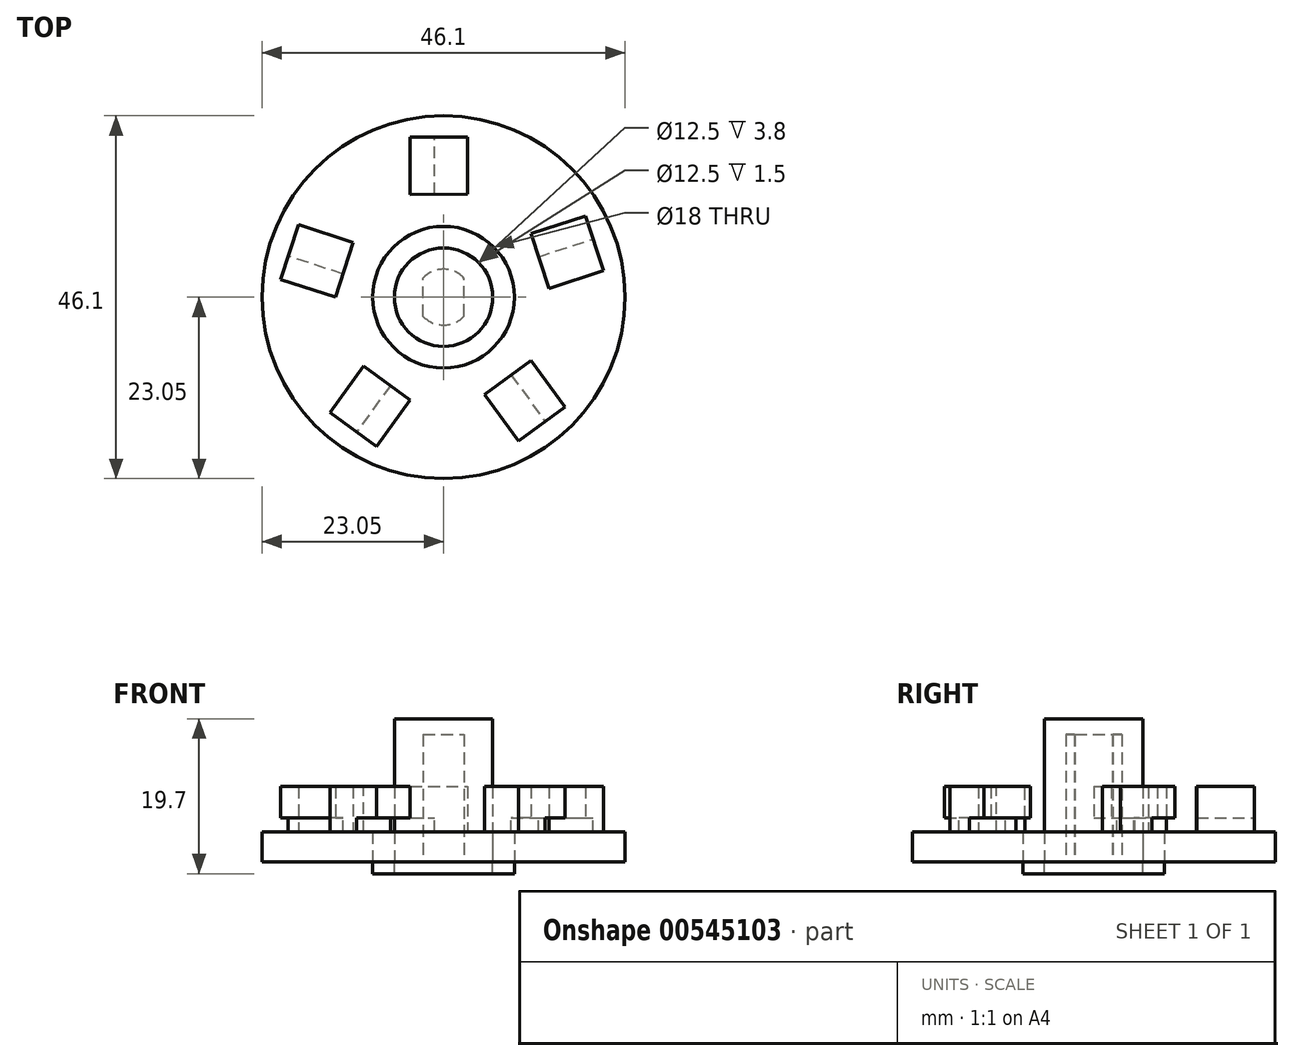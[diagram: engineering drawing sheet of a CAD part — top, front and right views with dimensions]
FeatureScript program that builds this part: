
annotation { "Feature Type Name" : "Feature", "Feature Type Description" : "" }
export const myFeature = defineFeature(function(context is Context, id is Id, definition is map)
    precondition{}
    {
        {
            var Q0;
            Q0=qCreatedBy(makeId("Top.planeOp"),FACE);
            var sketch = newSketch(context, id + "F0", { "sketchPlane" : qUnion([Q0])});
            skCircle(sketch, "E0", {"center": v(0, 0) * mm, "radius": 23.05 * mm});
            skCircle(sketch, "E1", {"center": v(0, 0) * mm, "radius": 6.25 * mm});
            skCircle(sketch, "E2", {"center": v(0, 0) * mm, "radius": 9 * mm});
            skLineSegment(sketch, "E3.left", {"start": v(-2.59, -2.43) * mm, "end": v(-2.59, 2.43) * mm});
            skLineSegment(sketch, "E3.right", {"start": v(2.62, -2.4) * mm, "end": v(2.62, 2.4) * mm});
            skArc(sketch, "E4", {"start": v(2.62, 2.4) * mm, "mid": v(0.03, 3.55) * mm, "end": v(-2.59, 2.43) * mm});
            skArc(sketch, "E5.trimOffspring", {"start": v(-2.59, -2.43) * mm, "mid": v(0.03, -3.55) * mm, "end": v(2.62, -2.4) * mm});
            skLineSegment(sketch, "E6", {"start": v(-1.36, -13.16) * mm, "end": v(-6.58, -20.37) * mm});
            skLineSegment(sketch, "E7", {"start": v(-6.58, -20.37) * mm, "end": v(-10.96, -17.2) * mm});
            skLineSegment(sketch, "E8", {"start": v(-10.96, -17.2) * mm, "end": v(-5.74, -10) * mm});
            skLineSegment(sketch, "E9", {"start": v(-5.74, -10) * mm, "end": v(-1.36, -13.16) * mm});
            skLineSegment(sketch, "E10", {"start": v(-12.94, -2.77) * mm, "end": v(-21.4, -0.04) * mm});
            skLineSegment(sketch, "E11", {"start": v(-21.4, -0.04) * mm, "end": v(-19.75, 5.1) * mm});
            skLineSegment(sketch, "E12", {"start": v(-19.75, 5.1) * mm, "end": v(-11.28, 2.37) * mm});
            skLineSegment(sketch, "E13", {"start": v(-11.28, 2.37) * mm, "end": v(-12.94, -2.77) * mm});
            skLineSegment(sketch, "E14", {"start": v(-6.63, 11.45) * mm, "end": v(-6.65, 20.35) * mm});
            skLineSegment(sketch, "E15", {"start": v(-6.65, 20.35) * mm, "end": v(-1.25, 20.36) * mm});
            skLineSegment(sketch, "E16", {"start": v(-1.25, 20.36) * mm, "end": v(-1.23, 11.46) * mm});
            skLineSegment(sketch, "E17", {"start": v(-1.23, 11.46) * mm, "end": v(-6.63, 11.45) * mm});
            skLineSegment(sketch, "E18", {"start": v(8.84, 9.85) * mm, "end": v(17.3, 12.61) * mm});
            skLineSegment(sketch, "E19", {"start": v(17.3, 12.61) * mm, "end": v(18.98, 7.48) * mm});
            skLineSegment(sketch, "E20", {"start": v(18.98, 7.48) * mm, "end": v(10.52, 4.71) * mm});
            skLineSegment(sketch, "E21", {"start": v(10.52, 4.71) * mm, "end": v(8.84, 9.85) * mm});
            skLineSegment(sketch, "E22", {"start": v(7.73, -8.55) * mm, "end": v(12.98, -15.74) * mm});
            skLineSegment(sketch, "E23", {"start": v(12.98, -15.74) * mm, "end": v(17.34, -12.55) * mm});
            skLineSegment(sketch, "E24", {"start": v(17.34, -12.55) * mm, "end": v(12.1, -5.36) * mm});
            skLineSegment(sketch, "E25", {"start": v(12.1, -5.36) * mm, "end": v(7.73, -8.55) * mm});
            skLineSegment(sketch, "E26", {"start": v(-19.75, 5.1) * mm, "end": v(-12.94, -2.77) * mm});
            skLineSegment(sketch, "E27", {"start": v(-11.28, 2.37) * mm, "end": v(-21.4, -0.04) * mm});
            skLineSegment(sketch, "E28", {"start": v(-6.65, 20.35) * mm, "end": v(-1.23, 11.46) * mm});
            skLineSegment(sketch, "E29", {"start": v(-6.63, 11.45) * mm, "end": v(-1.25, 20.36) * mm});
            skLineSegment(sketch, "E30", {"start": v(17.3, 12.61) * mm, "end": v(10.52, 4.71) * mm});
            skLineSegment(sketch, "E31", {"start": v(8.84, 9.85) * mm, "end": v(18.98, 7.48) * mm});
            skLineSegment(sketch, "E32", {"start": v(12.1, -5.36) * mm, "end": v(12.98, -15.74) * mm});
            skLineSegment(sketch, "E33", {"start": v(17.34, -12.55) * mm, "end": v(7.73, -8.55) * mm});
            skLineSegment(sketch, "E34", {"start": v(-1.36, -13.16) * mm, "end": v(-10.96, -17.2) * mm});
            skLineSegment(sketch, "E35", {"start": v(-5.74, -10) * mm, "end": v(-6.58, -20.37) * mm});
            skPoint(sketch, "E36", {"position": v(-16.34, 1.17) * mm});
            skPoint(sketch, "E37", {"position": v(-3.94, 15.9) * mm});
            skPoint(sketch, "E38", {"position": v(13.9, 8.66) * mm});
            skPoint(sketch, "E39", {"position": v(12.54, -10.55) * mm});
            skPoint(sketch, "E40", {"position": v(-6.16, -15.18) * mm});
            skLineSegment(sketch, "E41", {"start": v(-16.34, 1.17) * mm, "end": v(0, 0) * mm});
            skLineSegment(sketch, "E42", {"start": v(0, 0) * mm, "end": v(-6.16, -15.18) * mm});
            skLineSegment(sketch, "E43", {"start": v(0, 0) * mm, "end": v(12.54, -10.55) * mm});
            skLineSegment(sketch, "E44", {"start": v(0, 0) * mm, "end": v(13.9, 8.66) * mm});
            skLineSegment(sketch, "E45", {"start": v(0, 0) * mm, "end": v(-3.94, 15.9) * mm});
            skSolve(sketch);
        }
        {
            var Q0;
            Q0=makeQuery(id+"F0.imprint","IMPRINT",FACE,{"disambiguationData":[TD([[makeQuery(id+"F0.imprint","IMPRINT",EDGE,{"derivedFrom":sQuery(id+"F0.wireOp",EDGE,"E1")}),1.0]])]});
            var Q1;
            {var subQ1=sQuery(id+"F0.wireOp",EDGE,"E1");var subQ5=sQuery(id+"F0.wireOp",EDGE,"E45");var subQ6=makeQuery(id+"F0.imprint","INTERSECT",VERTEX,{"derivedFrom":[subQ1,subQ5]});Q1=makeQuery(id+"F0.imprint","IMPRINT",FACE,{"disambiguationData":[TD([[makeQuery(id+"F0.imprint","IMPRINT",EDGE,{"disambiguationData":[TD([[subQ6,1.0]])],"derivedFrom":subQ1}),1.0]])]});}
            var Q2;
            {var subQ1=sQuery(id+"F0.wireOp",EDGE,"E1");var subQ7=sQuery(id+"F0.wireOp",EDGE,"E45");var subQ9=makeQuery(id+"F0.imprint","INTERSECT",VERTEX,{"derivedFrom":[subQ1,subQ7]});Q2=makeQuery(id+"F0.imprint","IMPRINT",FACE,{"disambiguationData":[TD([[makeQuery(id+"F0.imprint","IMPRINT",EDGE,{"disambiguationData":[TD([[subQ9,-1.0]])],"derivedFrom":subQ1}),1.0]])]});}
            var Q3;
            {var subQ0=sQuery(id+"F0.wireOp",EDGE,"E41");var subQ1=sQuery(id+"F0.wireOp",EDGE,"E1");var subQ2=makeQuery(id+"F0.imprint","INTERSECT",VERTEX,{"derivedFrom":[subQ1,subQ0]});Q3=makeQuery(id+"F0.imprint","IMPRINT",FACE,{"disambiguationData":[TD([[makeQuery(id+"F0.imprint","IMPRINT",EDGE,{"disambiguationData":[TD([[subQ2,-1.0]])],"derivedFrom":subQ1}),1.0]])]});}
            var Q4;
            {var subQ0=sQuery(id+"F0.wireOp",EDGE,"E42");var subQ1=sQuery(id+"F0.wireOp",EDGE,"E1");var subQ2=makeQuery(id+"F0.imprint","INTERSECT",VERTEX,{"derivedFrom":[subQ1,subQ0]});Q4=makeQuery(id+"F0.imprint","IMPRINT",FACE,{"disambiguationData":[TD([[makeQuery(id+"F0.imprint","IMPRINT",EDGE,{"disambiguationData":[TD([[subQ2,-1.0]])],"derivedFrom":subQ1}),1.0]])]});}
            extrude(context, id + "F1", {"entities" : qUnion([Q0, Q1, Q2, Q3, Q4]), "depth" : 16.2 * mm, "offsetDistance" : 25 * mm});
        }
        {
            var Q0;
            Q0=makeQuery(id+"F0.imprint","IMPRINT",FACE,{"disambiguationData":[TD([[makeQuery(id+"F0.imprint","IMPRINT",EDGE,{"derivedFrom":sQuery(id+"F0.wireOp",EDGE,"E0")}),1.0]])]});
            extrude(context, id + "F2", {"entities" : qUnion([Q0]), "operationType" : NewBodyOperationType.ADD, "depth" : 3.8 * mm, "offsetDistance" : 25 * mm});
        }
        {
            var Q0;
            Q0=makeQuery(id+"F0.imprint","IMPRINT",FACE,{"disambiguationData":[TD([[makeQuery(id+"F0.imprint","IMPRINT",EDGE,{"derivedFrom":sQuery(id+"F0.wireOp",EDGE,"E1")}),-1.0]])]});
            extrude(context, id + "F3", {"entities" : qUnion([Q0]), "oppositeDirection" : true, "depth" : 1.5 * mm, "offsetDistance" : 25 * mm});
        }
        {
            var Q0;
            Q0=makeQuery(id+"F0.imprint","IMPRINT",FACE,{"disambiguationData":[TD([[makeQuery(id+"F0.imprint","IMPRINT",EDGE,{"derivedFrom":sQuery(id+"F0.wireOp",EDGE,"E1")}),-1.0]])]});
            extrude(context, id + "F4", {"entities" : qUnion([Q0]), "depth" : 3.8 * mm, "offsetDistance" : 25 * mm});
        }
        {
            var Q0;
            Q0=makeQuery(id+"F1.opExtrude","CAP_FACE",FACE,{"disambiguationData":[OSD([sQuery(id+"F0.wireOp",EDGE,"E1"),sQuery(id+"F0.wireOp",EDGE,"E3.left"),sQuery(id+"F0.wireOp",EDGE,"E3.right"),sQuery(id+"F0.wireOp",EDGE,"E4"),sQuery(id+"F0.wireOp",EDGE,"E5.trimOffspring")])],"isStart":false});
            var sketch = newSketch(context, id + "F5", { "sketchPlane" : qUnion([Q0])});
            skCircle(sketch, "E46", {"center": v(0, 0) * mm, "radius": 6.25 * mm});
            skSolve(sketch);
        }
        {
            var Q0;
            Q0=makeQuery(id+"F5.imprint","IMPRINT",FACE,{"disambiguationData":[TD([[makeQuery(id+"F5.imprint","IMPRINT",EDGE,{"derivedFrom":sQuery(id+"F5.wireOp",EDGE,"E46")}),1.0]])]});
            var Q1;
            Q1=makeQuery(id+"F5.imprint","IMPRINT",FACE,{"disambiguationData":[TD([[makeQuery(id+"F5.imprint","IMPRINT",EDGE,{"derivedFrom":makeQuery(id+"F1.opExtrude","CAP_EDGE",EDGE,{"disambiguationData":[OSD([sQuery(id+"F0.wireOp",EDGE,"E3.left")])],"isStart":false})}),-1.0]])]});
            extrude(context, id + "F6", {"entities" : qUnion([Q0, Q1]), "operationType" : NewBodyOperationType.ADD, "depth" : 2 * mm, "offsetDistance" : 25 * mm});
        }
        {
            var Q0;
            {var subQ0=sQuery(id+"F0.wireOp",EDGE,"E10");Q0=makeQuery(id+"F0.imprint","IMPRINT",FACE,{"disambiguationData":[TD([[makeQuery(id+"F0.imprint","IMPRINT",EDGE,{"derivedFrom":subQ0}),-1.0]])]});}
            var Q1;
            {var subQ1=sQuery(id+"F0.wireOp",EDGE,"E13");var subQ3=sQuery(id+"F0.wireOp",EDGE,"E41");var subQ4=makeQuery(id+"F0.imprint","INTERSECT",VERTEX,{"derivedFrom":[subQ1,subQ3]});Q1=makeQuery(id+"F0.imprint","IMPRINT",FACE,{"disambiguationData":[TD([[makeQuery(id+"F0.imprint","IMPRINT",EDGE,{"disambiguationData":[TD([[subQ4,-1.0]])],"derivedFrom":subQ1}),-1.0]])]});}
            var Q2;
            {var subQ0=sQuery(id+"F0.wireOp",EDGE,"E11");Q2=makeQuery(id+"F0.imprint","IMPRINT",FACE,{"disambiguationData":[TD([[makeQuery(id+"F0.imprint","IMPRINT",EDGE,{"derivedFrom":subQ0}),-1.0]])]});}
            var Q3;
            {var subQ0=sQuery(id+"F0.wireOp",EDGE,"E12");Q3=makeQuery(id+"F0.imprint","IMPRINT",FACE,{"disambiguationData":[TD([[makeQuery(id+"F0.imprint","IMPRINT",EDGE,{"derivedFrom":subQ0}),-1.0]])]});}
            var Q4;
            {var subQ1=sQuery(id+"F0.wireOp",EDGE,"E13");var subQ3=sQuery(id+"F0.wireOp",EDGE,"E41");var subQ4=makeQuery(id+"F0.imprint","INTERSECT",VERTEX,{"derivedFrom":[subQ1,subQ3]});Q4=makeQuery(id+"F0.imprint","IMPRINT",FACE,{"disambiguationData":[TD([[makeQuery(id+"F0.imprint","IMPRINT",EDGE,{"disambiguationData":[TD([[subQ4,1.0]])],"derivedFrom":subQ1}),-1.0]])]});}
            var Q5;
            {var subQ0=sQuery(id+"F0.wireOp",EDGE,"E7");Q5=makeQuery(id+"F0.imprint","IMPRINT",FACE,{"disambiguationData":[TD([[makeQuery(id+"F0.imprint","IMPRINT",EDGE,{"derivedFrom":subQ0}),-1.0]])]});}
            var Q6;
            {var subQ0=sQuery(id+"F0.wireOp",EDGE,"E8");Q6=makeQuery(id+"F0.imprint","IMPRINT",FACE,{"disambiguationData":[TD([[makeQuery(id+"F0.imprint","IMPRINT",EDGE,{"derivedFrom":subQ0}),-1.0]])]});}
            var Q7;
            {var subQ0=sQuery(id+"F0.wireOp",EDGE,"E6");Q7=makeQuery(id+"F0.imprint","IMPRINT",FACE,{"disambiguationData":[TD([[makeQuery(id+"F0.imprint","IMPRINT",EDGE,{"derivedFrom":subQ0}),-1.0]])]});}
            var Q8;
            {var subQ1=sQuery(id+"F0.wireOp",EDGE,"E9");var subQ3=sQuery(id+"F0.wireOp",EDGE,"E42");var subQ4=makeQuery(id+"F0.imprint","INTERSECT",VERTEX,{"derivedFrom":[subQ1,subQ3]});Q8=makeQuery(id+"F0.imprint","IMPRINT",FACE,{"disambiguationData":[TD([[makeQuery(id+"F0.imprint","IMPRINT",EDGE,{"disambiguationData":[TD([[subQ4,-1.0]])],"derivedFrom":subQ1}),-1.0]])]});}
            var Q9;
            {var subQ1=sQuery(id+"F0.wireOp",EDGE,"E9");var subQ3=sQuery(id+"F0.wireOp",EDGE,"E42");var subQ4=makeQuery(id+"F0.imprint","INTERSECT",VERTEX,{"derivedFrom":[subQ1,subQ3]});Q9=makeQuery(id+"F0.imprint","IMPRINT",FACE,{"disambiguationData":[TD([[makeQuery(id+"F0.imprint","IMPRINT",EDGE,{"disambiguationData":[TD([[subQ4,1.0]])],"derivedFrom":subQ1}),-1.0]])]});}
            var Q10;
            {var subQ0=sQuery(id+"F0.wireOp",EDGE,"E22");Q10=makeQuery(id+"F0.imprint","IMPRINT",FACE,{"disambiguationData":[TD([[makeQuery(id+"F0.imprint","IMPRINT",EDGE,{"derivedFrom":subQ0}),1.0]])]});}
            var Q11;
            {var subQ0=sQuery(id+"F0.wireOp",EDGE,"E23");Q11=makeQuery(id+"F0.imprint","IMPRINT",FACE,{"disambiguationData":[TD([[makeQuery(id+"F0.imprint","IMPRINT",EDGE,{"derivedFrom":subQ0}),1.0]])]});}
            var Q12;
            {var subQ0=sQuery(id+"F0.wireOp",EDGE,"E24");Q12=makeQuery(id+"F0.imprint","IMPRINT",FACE,{"disambiguationData":[TD([[makeQuery(id+"F0.imprint","IMPRINT",EDGE,{"derivedFrom":subQ0}),1.0]])]});}
            var Q13;
            {var subQ1=sQuery(id+"F0.wireOp",EDGE,"E25");var subQ3=sQuery(id+"F0.wireOp",EDGE,"E43");var subQ4=makeQuery(id+"F0.imprint","INTERSECT",VERTEX,{"derivedFrom":[subQ1,subQ3]});Q13=makeQuery(id+"F0.imprint","IMPRINT",FACE,{"disambiguationData":[TD([[makeQuery(id+"F0.imprint","IMPRINT",EDGE,{"disambiguationData":[TD([[subQ4,1.0]])],"derivedFrom":subQ1}),1.0]])]});}
            var Q14;
            {var subQ1=sQuery(id+"F0.wireOp",EDGE,"E25");var subQ3=sQuery(id+"F0.wireOp",EDGE,"E43");var subQ4=makeQuery(id+"F0.imprint","INTERSECT",VERTEX,{"derivedFrom":[subQ1,subQ3]});Q14=makeQuery(id+"F0.imprint","IMPRINT",FACE,{"disambiguationData":[TD([[makeQuery(id+"F0.imprint","IMPRINT",EDGE,{"disambiguationData":[TD([[subQ4,-1.0]])],"derivedFrom":subQ1}),1.0]])]});}
            var Q15;
            {var subQ0=sQuery(id+"F0.wireOp",EDGE,"E20");Q15=makeQuery(id+"F0.imprint","IMPRINT",FACE,{"disambiguationData":[TD([[makeQuery(id+"F0.imprint","IMPRINT",EDGE,{"derivedFrom":subQ0}),-1.0]])]});}
            var Q16;
            {var subQ1=sQuery(id+"F0.wireOp",EDGE,"E21");var subQ3=sQuery(id+"F0.wireOp",EDGE,"E44");var subQ4=makeQuery(id+"F0.imprint","INTERSECT",VERTEX,{"derivedFrom":[subQ1,subQ3]});Q16=makeQuery(id+"F0.imprint","IMPRINT",FACE,{"disambiguationData":[TD([[makeQuery(id+"F0.imprint","IMPRINT",EDGE,{"disambiguationData":[TD([[subQ4,1.0]])],"derivedFrom":subQ1}),-1.0]])]});}
            var Q17;
            {var subQ1=sQuery(id+"F0.wireOp",EDGE,"E21");var subQ3=sQuery(id+"F0.wireOp",EDGE,"E44");var subQ4=makeQuery(id+"F0.imprint","INTERSECT",VERTEX,{"derivedFrom":[subQ1,subQ3]});Q17=makeQuery(id+"F0.imprint","IMPRINT",FACE,{"disambiguationData":[TD([[makeQuery(id+"F0.imprint","IMPRINT",EDGE,{"disambiguationData":[TD([[subQ4,-1.0]])],"derivedFrom":subQ1}),-1.0]])]});}
            var Q18;
            {var subQ0=sQuery(id+"F0.wireOp",EDGE,"E18");Q18=makeQuery(id+"F0.imprint","IMPRINT",FACE,{"disambiguationData":[TD([[makeQuery(id+"F0.imprint","IMPRINT",EDGE,{"derivedFrom":subQ0}),-1.0]])]});}
            var Q19;
            {var subQ0=sQuery(id+"F0.wireOp",EDGE,"E19");Q19=makeQuery(id+"F0.imprint","IMPRINT",FACE,{"disambiguationData":[TD([[makeQuery(id+"F0.imprint","IMPRINT",EDGE,{"derivedFrom":subQ0}),-1.0]])]});}
            var Q20;
            {var subQ1=sQuery(id+"F0.wireOp",EDGE,"E17");var subQ3=sQuery(id+"F0.wireOp",EDGE,"E45");var subQ4=makeQuery(id+"F0.imprint","INTERSECT",VERTEX,{"derivedFrom":[subQ1,subQ3]});Q20=makeQuery(id+"F0.imprint","IMPRINT",FACE,{"disambiguationData":[TD([[makeQuery(id+"F0.imprint","IMPRINT",EDGE,{"disambiguationData":[TD([[subQ4,-1.0]])],"derivedFrom":subQ1}),-1.0]])]});}
            var Q21;
            {var subQ1=sQuery(id+"F0.wireOp",EDGE,"E17");var subQ3=sQuery(id+"F0.wireOp",EDGE,"E45");var subQ4=makeQuery(id+"F0.imprint","INTERSECT",VERTEX,{"derivedFrom":[subQ1,subQ3]});Q21=makeQuery(id+"F0.imprint","IMPRINT",FACE,{"disambiguationData":[TD([[makeQuery(id+"F0.imprint","IMPRINT",EDGE,{"disambiguationData":[TD([[subQ4,1.0]])],"derivedFrom":subQ1}),-1.0]])]});}
            var Q22;
            {var subQ0=sQuery(id+"F0.wireOp",EDGE,"E16");Q22=makeQuery(id+"F0.imprint","IMPRINT",FACE,{"disambiguationData":[TD([[makeQuery(id+"F0.imprint","IMPRINT",EDGE,{"derivedFrom":subQ0}),-1.0]])]});}
            var Q23;
            {var subQ0=sQuery(id+"F0.wireOp",EDGE,"E15");Q23=makeQuery(id+"F0.imprint","IMPRINT",FACE,{"disambiguationData":[TD([[makeQuery(id+"F0.imprint","IMPRINT",EDGE,{"derivedFrom":subQ0}),-1.0]])]});}
            var Q24;
            {var subQ0=sQuery(id+"F0.wireOp",EDGE,"E14");Q24=makeQuery(id+"F0.imprint","IMPRINT",FACE,{"disambiguationData":[TD([[makeQuery(id+"F0.imprint","IMPRINT",EDGE,{"derivedFrom":subQ0}),-1.0]])]});}
            extrude(context, id + "F7", {"entities" : qUnion([Q0, Q1, Q2, Q3, Q4, Q5, Q6, Q7, Q8, Q9, Q10, Q11, Q12, Q13, Q14, Q15, Q16, Q17, Q18, Q19, Q20, Q21, Q22, Q23, Q24]), "operationType" : NewBodyOperationType.ADD, "depth" : 9.6 * mm, "offsetDistance" : 25 * mm});
        }
        {
            var Q0;
            Q0=makeQuery(id+"F7.opExtrude","SWEPT_FACE",FACE,{"disambiguationData":[OSD([sQuery(id+"F0.wireOp",EDGE,"E12")])]});
            var sketch = newSketch(context, id + "F8", { "sketchPlane" : qUnion([Q0])});
            skLineSegment(sketch, "E47.bottom", {"start": v(20.36, 9.6) * mm, "end": v(13.06, 9.6) * mm});
            skLineSegment(sketch, "E47.top", {"start": v(20.36, 3.8) * mm, "end": v(13.06, 3.8) * mm});
            skLineSegment(sketch, "E47.left", {"start": v(20.36, 9.6) * mm, "end": v(20.36, 3.8) * mm});
            skLineSegment(sketch, "E47.right", {"start": v(13.06, 9.6) * mm, "end": v(13.06, 3.8) * mm});
            skLineSegment(sketch, "E48.bottom", {"start": v(11.46, 9.6) * mm, "end": v(13.06, 9.6) * mm});
            skLineSegment(sketch, "E48.top", {"start": v(11.46, 3.8) * mm, "end": v(13.06, 3.8) * mm});
            skLineSegment(sketch, "E48.left", {"start": v(11.46, 9.6) * mm, "end": v(11.46, 3.8) * mm});
            skSolve(sketch);
        }
        {
            var Q0;
            Q0=makeQuery(id+"F8.imprint","IMPRINT",FACE,{"disambiguationData":[TD([[makeQuery(id+"F8.imprint","IMPRINT",EDGE,{"derivedFrom":sQuery(id+"F8.wireOp",EDGE,"E48.bottom")}),1.0]])]});
            extrude(context, id + "F9", {"entities" : qUnion([Q0]), "operationType" : NewBodyOperationType.REMOVE, "oppositeDirection" : true, "depth" : 5.4 * mm, "offsetDistance" : 25 * mm});
        }
        {
            var Q0;
            Q0=makeQuery(id+"F8.imprint","IMPRINT",FACE,{"disambiguationData":[TD([[makeQuery(id+"F8.imprint","IMPRINT",EDGE,{"derivedFrom":sQuery(id+"F8.wireOp",EDGE,"E47.bottom")}),1.0]])]});
            extrude(context, id + "F10", {"entities" : qUnion([Q0]), "operationType" : NewBodyOperationType.ADD, "depth" : 4.3 * mm, "offsetDistance" : 25 * mm});
        }
        {
            var Q0;
            Q0=makeQuery(id+"F10.boolean.opBoolean","MERGE",FACE,{"derivedFrom":[makeQuery(id+"F7.opExtrude","SWEPT_FACE",FACE,{"disambiguationData":[OSD([sQuery(id+"F0.wireOp",EDGE,"E11")])]}),makeQuery(id+"F10.opExtrude","SWEPT_FACE",FACE,{"disambiguationData":[OSD([sQuery(id+"F8.wireOp",EDGE,"E47.left")])]})]});
            var sketch = newSketch(context, id + "F11", { "sketchPlane" : qUnion([Q0])});
            skLineSegment(sketch, "E49.bottom", {"start": v(6.61, 3.8) * mm, "end": v(1.11, 3.8) * mm});
            skLineSegment(sketch, "E49.top", {"start": v(6.61, 5.6) * mm, "end": v(1.11, 5.6) * mm});
            skLineSegment(sketch, "E49.left", {"start": v(6.61, 3.8) * mm, "end": v(6.61, 5.6) * mm});
            skLineSegment(sketch, "E49.right", {"start": v(1.11, 3.8) * mm, "end": v(1.11, 5.6) * mm});
            skLineSegment(sketch, "E50.bottom", {"start": v(6.61, 9.6) * mm, "end": v(4.21, 9.6) * mm});
            skLineSegment(sketch, "E50.top", {"start": v(6.61, 5.6) * mm, "end": v(4.21, 5.6) * mm});
            skLineSegment(sketch, "E50.left", {"start": v(6.61, 9.6) * mm, "end": v(6.61, 5.6) * mm});
            skLineSegment(sketch, "E50.right", {"start": v(4.21, 9.6) * mm, "end": v(4.21, 5.6) * mm});
            skSolve(sketch);
        }
        {
            var Q0;
            Q0=makeQuery(id+"F11.imprint","IMPRINT",FACE,{"disambiguationData":[TD([[makeQuery(id+"F11.imprint","IMPRINT",EDGE,{"derivedFrom":sQuery(id+"F11.wireOp",EDGE,"E49.bottom")}),-1.0]])]});
            extrude(context, id + "F12", {"entities" : qUnion([Q0]), "operationType" : NewBodyOperationType.REMOVE, "oppositeDirection" : true, "depth" : 7.3 * mm, "offsetDistance" : 25 * mm});
        }
        {
            var Q0;
            Q0=makeQuery(id+"F11.imprint","IMPRINT",FACE,{"disambiguationData":[TD([[makeQuery(id+"F11.imprint","IMPRINT",EDGE,{"derivedFrom":sQuery(id+"F11.wireOp",EDGE,"E50.bottom")}),1.0]])]});
            extrude(context, id + "F13", {"entities" : qUnion([Q0]), "operationType" : NewBodyOperationType.REMOVE, "oppositeDirection" : true, "depth" : 7.3 * mm, "offsetDistance" : 25 * mm});
        }
        {
            var Q0;
            Q0=makeQuery(id+"F7.opExtrude","SWEPT_FACE",FACE,{"disambiguationData":[OSD([sQuery(id+"F0.wireOp",EDGE,"E16")])]});
            var sketch = newSketch(context, id + "F14", { "sketchPlane" : qUnion([Q0])});
            skLineSegment(sketch, "E51.bottom", {"start": v(20.36, 9.6) * mm, "end": v(13.06, 9.6) * mm});
            skLineSegment(sketch, "E51.top", {"start": v(20.36, 3.8) * mm, "end": v(13.06, 3.8) * mm});
            skLineSegment(sketch, "E51.left", {"start": v(20.36, 9.6) * mm, "end": v(20.36, 3.8) * mm});
            skLineSegment(sketch, "E51.right", {"start": v(13.06, 9.6) * mm, "end": v(13.06, 3.8) * mm});
            skLineSegment(sketch, "E52.bottom", {"start": v(13.06, 9.6) * mm, "end": v(11.46, 9.6) * mm});
            skLineSegment(sketch, "E52.top", {"start": v(13.06, 9.6) * mm, "end": v(11.46, 9.6) * mm});
            skLineSegment(sketch, "E52.left", {"start": v(13.06, 9.6) * mm, "end": v(13.06, 9.6) * mm});
            skLineSegment(sketch, "E52.right", {"start": v(11.46, 9.6) * mm, "end": v(11.46, 9.6) * mm});
            skLineSegment(sketch, "E53.bottom", {"start": v(11.46, 3.8) * mm, "end": v(13.06, 3.8) * mm});
            skLineSegment(sketch, "E53.top", {"start": v(11.46, 9.6) * mm, "end": v(13.06, 9.6) * mm});
            skLineSegment(sketch, "E53.left", {"start": v(11.46, 3.8) * mm, "end": v(11.46, 9.6) * mm});
            skLineSegment(sketch, "E53.right", {"start": v(13.06, 3.8) * mm, "end": v(13.06, 9.6) * mm});
            skSolve(sketch);
        }
        {
            var Q0;
            Q0=makeQuery(id+"F14.imprint","IMPRINT",FACE,{"disambiguationData":[TD([[makeQuery(id+"F14.imprint","IMPRINT",EDGE,{"derivedFrom":sQuery(id+"F14.wireOp",EDGE,"E53.bottom")}),-1.0]])]});
            extrude(context, id + "F15", {"entities" : qUnion([Q0]), "operationType" : NewBodyOperationType.REMOVE, "oppositeDirection" : true, "depth" : 5.4 * mm, "offsetDistance" : 25 * mm});
        }
        {
            var Q0;
            Q0=makeQuery(id+"F7.opExtrude","SWEPT_FACE",FACE,{"disambiguationData":[OSD([sQuery(id+"F0.wireOp",EDGE,"E16")])]});
            extrude(context, id + "F16", {"entities" : qUnion([Q0]), "operationType" : NewBodyOperationType.ADD, "depth" : 4.3 * mm, "offsetDistance" : 25 * mm});
        }
        {
            var Q0;
            {var subQ0=sQuery(id+"F0.wireOp",EDGE,"E15");Q0=makeQuery(id+"F16.boolean.opBoolean","MERGE",FACE,{"derivedFrom":[makeQuery(id+"F7.opExtrude","SWEPT_FACE",FACE,{"disambiguationData":[OSD([subQ0])]}),makeQuery(id+"F16.opExtrude","SWEPT_FACE",FACE,{"disambiguationData":[OSD([subQ0,sQuery(id+"F0.wireOp",EDGE,"E16"),sQuery(id+"F0.wireOp",EDGE,"E29")])]})]});}
            var sketch = newSketch(context, id + "F17", { "sketchPlane" : qUnion([Q0])});
            skLineSegment(sketch, "E54.bottom", {"start": v(6.61, 3.8) * mm, "end": v(1.11, 3.8) * mm});
            skLineSegment(sketch, "E54.top", {"start": v(6.61, 5.6) * mm, "end": v(1.11, 5.6) * mm});
            skLineSegment(sketch, "E54.left", {"start": v(6.61, 3.8) * mm, "end": v(6.61, 5.6) * mm});
            skLineSegment(sketch, "E54.right", {"start": v(1.11, 3.8) * mm, "end": v(1.11, 5.6) * mm});
            skLineSegment(sketch, "E55.bottom", {"start": v(6.61, 9.6) * mm, "end": v(4.21, 9.6) * mm});
            skLineSegment(sketch, "E55.top", {"start": v(6.61, 5.6) * mm, "end": v(4.21, 5.6) * mm});
            skLineSegment(sketch, "E55.left", {"start": v(6.61, 9.6) * mm, "end": v(6.61, 5.6) * mm});
            skLineSegment(sketch, "E55.right", {"start": v(4.21, 9.6) * mm, "end": v(4.21, 5.6) * mm});
            skSolve(sketch);
        }
        {
            var Q0;
            Q0=makeQuery(id+"F17.imprint","IMPRINT",FACE,{"disambiguationData":[TD([[makeQuery(id+"F17.imprint","IMPRINT",EDGE,{"derivedFrom":sQuery(id+"F17.wireOp",EDGE,"E54.bottom")}),-1.0]])]});
            var Q1;
            Q1=makeQuery(id+"F17.imprint","IMPRINT",FACE,{"disambiguationData":[TD([[makeQuery(id+"F17.imprint","IMPRINT",EDGE,{"derivedFrom":sQuery(id+"F17.wireOp",EDGE,"E55.bottom")}),1.0]])]});
            extrude(context, id + "F18", {"entities" : qUnion([Q0, Q1]), "operationType" : NewBodyOperationType.REMOVE, "oppositeDirection" : true, "depth" : 7.3 * mm, "offsetDistance" : 25 * mm});
        }
        {
            var Q0;
            Q0=makeQuery(id+"F7.opExtrude","SWEPT_FACE",FACE,{"disambiguationData":[OSD([sQuery(id+"F0.wireOp",EDGE,"E20")])]});
            var sketch = newSketch(context, id + "F19", { "sketchPlane" : qUnion([Q0])});
            skLineSegment(sketch, "E56.bottom", {"start": v(20.36, 9.6) * mm, "end": v(13.06, 9.6) * mm});
            skLineSegment(sketch, "E56.top", {"start": v(20.36, 3.8) * mm, "end": v(13.06, 3.8) * mm});
            skLineSegment(sketch, "E56.left", {"start": v(20.36, 9.6) * mm, "end": v(20.36, 3.8) * mm});
            skLineSegment(sketch, "E56.right", {"start": v(13.06, 9.6) * mm, "end": v(13.06, 3.8) * mm});
            skLineSegment(sketch, "E57.bottom", {"start": v(13.06, 9.6) * mm, "end": v(11.46, 9.6) * mm});
            skLineSegment(sketch, "E57.top", {"start": v(13.06, 3.8) * mm, "end": v(11.46, 3.8) * mm});
            skLineSegment(sketch, "E57.right", {"start": v(11.46, 9.6) * mm, "end": v(11.46, 3.8) * mm});
            skSolve(sketch);
        }
        {
            var Q0;
            Q0=makeQuery(id+"F19.imprint","IMPRINT",FACE,{"disambiguationData":[TD([[makeQuery(id+"F19.imprint","IMPRINT",EDGE,{"derivedFrom":sQuery(id+"F19.wireOp",EDGE,"E57.bottom")}),1.0]])]});
            extrude(context, id + "F20", {"entities" : qUnion([Q0]), "operationType" : NewBodyOperationType.REMOVE, "oppositeDirection" : true, "depth" : 5.4 * mm, "offsetDistance" : 25 * mm});
        }
        {
            var Q0;
            Q0=makeQuery(id+"F19.imprint","IMPRINT",FACE,{"disambiguationData":[TD([[makeQuery(id+"F19.imprint","IMPRINT",EDGE,{"derivedFrom":sQuery(id+"F19.wireOp",EDGE,"E56.bottom")}),1.0]])]});
            extrude(context, id + "F21", {"entities" : qUnion([Q0]), "operationType" : NewBodyOperationType.ADD, "depth" : 4.3 * mm, "offsetDistance" : 25 * mm});
        }
        {
            var Q0;
            Q0=makeQuery(id+"F21.boolean.opBoolean","MERGE",FACE,{"derivedFrom":[makeQuery(id+"F7.opExtrude","SWEPT_FACE",FACE,{"disambiguationData":[OSD([sQuery(id+"F0.wireOp",EDGE,"E19")])]}),makeQuery(id+"F21.opExtrude","SWEPT_FACE",FACE,{"disambiguationData":[OSD([sQuery(id+"F19.wireOp",EDGE,"E56.left")])]})]});
            var sketch = newSketch(context, id + "F22", { "sketchPlane" : qUnion([Q0])});
            skLineSegment(sketch, "E58.bottom", {"start": v(6.61, 3.8) * mm, "end": v(1.11, 3.8) * mm});
            skLineSegment(sketch, "E58.top", {"start": v(6.61, 5.6) * mm, "end": v(1.11, 5.6) * mm});
            skLineSegment(sketch, "E58.left", {"start": v(6.61, 3.8) * mm, "end": v(6.61, 5.6) * mm});
            skLineSegment(sketch, "E58.right", {"start": v(1.11, 3.8) * mm, "end": v(1.11, 5.6) * mm});
            skLineSegment(sketch, "E59.bottom", {"start": v(6.61, 9.6) * mm, "end": v(4.21, 9.6) * mm});
            skLineSegment(sketch, "E59.top", {"start": v(6.61, 5.6) * mm, "end": v(4.21, 5.6) * mm});
            skLineSegment(sketch, "E59.left", {"start": v(6.61, 9.6) * mm, "end": v(6.61, 5.6) * mm});
            skLineSegment(sketch, "E59.right", {"start": v(4.21, 9.6) * mm, "end": v(4.21, 5.6) * mm});
            skSolve(sketch);
        }
        {
            var Q0;
            Q0=makeQuery(id+"F22.imprint","IMPRINT",FACE,{"disambiguationData":[TD([[makeQuery(id+"F22.imprint","IMPRINT",EDGE,{"derivedFrom":sQuery(id+"F22.wireOp",EDGE,"E59.bottom")}),1.0]])]});
            var Q1;
            Q1=makeQuery(id+"F22.imprint","IMPRINT",FACE,{"disambiguationData":[TD([[makeQuery(id+"F22.imprint","IMPRINT",EDGE,{"derivedFrom":sQuery(id+"F22.wireOp",EDGE,"E58.bottom")}),-1.0]])]});
            extrude(context, id + "F23", {"entities" : qUnion([Q0, Q1]), "operationType" : NewBodyOperationType.REMOVE, "oppositeDirection" : true, "depth" : 7.3 * mm, "offsetDistance" : 25 * mm});
        }
        {
            var Q0;
            Q0=makeQuery(id+"F7.opExtrude","SWEPT_FACE",FACE,{"disambiguationData":[OSD([sQuery(id+"F0.wireOp",EDGE,"E22")])]});
            var sketch = newSketch(context, id + "F24", { "sketchPlane" : qUnion([Q0])});
            skLineSegment(sketch, "E60.bottom", {"start": v(20.36, 3.8) * mm, "end": v(13.06, 3.8) * mm});
            skLineSegment(sketch, "E60.top", {"start": v(20.36, 9.6) * mm, "end": v(13.06, 9.6) * mm});
            skLineSegment(sketch, "E60.left", {"start": v(20.36, 3.8) * mm, "end": v(20.36, 9.6) * mm});
            skLineSegment(sketch, "E60.right", {"start": v(13.06, 3.8) * mm, "end": v(13.06, 9.6) * mm});
            skLineSegment(sketch, "E61.bottom", {"start": v(13.06, 9.6) * mm, "end": v(11.46, 9.6) * mm});
            skLineSegment(sketch, "E61.top", {"start": v(13.06, 3.8) * mm, "end": v(11.46, 3.8) * mm});
            skLineSegment(sketch, "E61.left", {"start": v(13.06, 9.6) * mm, "end": v(13.06, 3.8) * mm});
            skLineSegment(sketch, "E61.right", {"start": v(11.46, 9.6) * mm, "end": v(11.46, 3.8) * mm});
            skSolve(sketch);
        }
        {
            var Q0;
            Q0=makeQuery(id+"F24.imprint","IMPRINT",FACE,{"disambiguationData":[TD([[makeQuery(id+"F24.imprint","IMPRINT",EDGE,{"derivedFrom":sQuery(id+"F24.wireOp",EDGE,"E61.bottom")}),-1.0]])]});
            extrude(context, id + "F25", {"entities" : qUnion([Q0]), "operationType" : NewBodyOperationType.REMOVE, "oppositeDirection" : true, "depth" : 5.4 * mm, "offsetDistance" : 25 * mm});
        }
        {
            var Q0;
            Q0=makeQuery(id+"F7.opExtrude","SWEPT_FACE",FACE,{"disambiguationData":[OSD([sQuery(id+"F0.wireOp",EDGE,"E22")])]});
            extrude(context, id + "F26", {"entities" : qUnion([Q0]), "operationType" : NewBodyOperationType.ADD, "depth" : 4.3 * mm, "offsetDistance" : 25 * mm});
        }
        {
            var Q0;
            {var subQ0=sQuery(id+"F0.wireOp",EDGE,"E23");Q0=makeQuery(id+"F26.boolean.opBoolean","MERGE",FACE,{"derivedFrom":[makeQuery(id+"F7.opExtrude","SWEPT_FACE",FACE,{"disambiguationData":[OSD([subQ0])]}),makeQuery(id+"F26.opExtrude","SWEPT_FACE",FACE,{"disambiguationData":[OSD([sQuery(id+"F0.wireOp",EDGE,"E22"),subQ0,sQuery(id+"F0.wireOp",EDGE,"E32")])]})]});}
            var sketch = newSketch(context, id + "F27", { "sketchPlane" : qUnion([Q0])});
            skLineSegment(sketch, "E62.bottom", {"start": v(6.61, 3.8) * mm, "end": v(1.11, 3.8) * mm});
            skLineSegment(sketch, "E62.top", {"start": v(6.61, 5.6) * mm, "end": v(1.11, 5.6) * mm});
            skLineSegment(sketch, "E62.left", {"start": v(6.61, 3.8) * mm, "end": v(6.61, 5.6) * mm});
            skLineSegment(sketch, "E62.right", {"start": v(1.11, 3.8) * mm, "end": v(1.11, 5.6) * mm});
            skLineSegment(sketch, "E63.bottom", {"start": v(6.61, 9.6) * mm, "end": v(4.21, 9.6) * mm});
            skLineSegment(sketch, "E63.top", {"start": v(6.61, 5.6) * mm, "end": v(4.21, 5.6) * mm});
            skLineSegment(sketch, "E63.left", {"start": v(6.61, 9.6) * mm, "end": v(6.61, 5.6) * mm});
            skLineSegment(sketch, "E63.right", {"start": v(4.21, 9.6) * mm, "end": v(4.21, 5.6) * mm});
            skSolve(sketch);
        }
        {
            var Q0;
            Q0=makeQuery(id+"F27.imprint","IMPRINT",FACE,{"disambiguationData":[TD([[makeQuery(id+"F27.imprint","IMPRINT",EDGE,{"derivedFrom":sQuery(id+"F27.wireOp",EDGE,"E63.bottom")}),-1.0]])]});
            var Q1;
            Q1=makeQuery(id+"F27.imprint","IMPRINT",FACE,{"disambiguationData":[TD([[makeQuery(id+"F27.imprint","IMPRINT",EDGE,{"derivedFrom":sQuery(id+"F27.wireOp",EDGE,"E62.bottom")}),1.0]])]});
            extrude(context, id + "F28", {"entities" : qUnion([Q0, Q1]), "operationType" : NewBodyOperationType.REMOVE, "oppositeDirection" : true, "depth" : 7.3 * mm, "offsetDistance" : 25 * mm});
        }
        {
            var Q0;
            Q0=makeQuery(id+"F7.opExtrude","SWEPT_FACE",FACE,{"disambiguationData":[OSD([sQuery(id+"F0.wireOp",EDGE,"E8")])]});
            var sketch = newSketch(context, id + "F29", { "sketchPlane" : qUnion([Q0])});
            skLineSegment(sketch, "E64.bottom", {"start": v(20.36, 3.8) * mm, "end": v(13.06, 3.8) * mm});
            skLineSegment(sketch, "E64.top", {"start": v(20.36, 9.6) * mm, "end": v(13.06, 9.6) * mm});
            skLineSegment(sketch, "E64.left", {"start": v(20.36, 3.8) * mm, "end": v(20.36, 9.6) * mm});
            skLineSegment(sketch, "E64.right", {"start": v(13.06, 3.8) * mm, "end": v(13.06, 9.6) * mm});
            skLineSegment(sketch, "E65.bottom", {"start": v(13.06, 9.6) * mm, "end": v(11.46, 9.6) * mm});
            skLineSegment(sketch, "E65.top", {"start": v(13.06, 3.8) * mm, "end": v(11.46, 3.8) * mm});
            skLineSegment(sketch, "E65.left", {"start": v(13.06, 9.6) * mm, "end": v(13.06, 3.8) * mm});
            skLineSegment(sketch, "E65.right", {"start": v(11.46, 9.6) * mm, "end": v(11.46, 3.8) * mm});
            skSolve(sketch);
        }
        {
            var Q0;
            Q0=makeQuery(id+"F29.imprint","IMPRINT",FACE,{"disambiguationData":[TD([[makeQuery(id+"F29.imprint","IMPRINT",EDGE,{"derivedFrom":sQuery(id+"F29.wireOp",EDGE,"E65.bottom")}),1.0]])]});
            extrude(context, id + "F30", {"entities" : qUnion([Q0]), "operationType" : NewBodyOperationType.REMOVE, "oppositeDirection" : true, "depth" : 5.4 * mm, "offsetDistance" : 25 * mm});
        }
        {
            var Q0;
            Q0=makeQuery(id+"F7.opExtrude","SWEPT_FACE",FACE,{"disambiguationData":[OSD([sQuery(id+"F0.wireOp",EDGE,"E8")])]});
            extrude(context, id + "F31", {"entities" : qUnion([Q0]), "operationType" : NewBodyOperationType.ADD, "depth" : 4.3 * mm, "offsetDistance" : 25 * mm});
        }
        {
            var Q0;
            {var subQ0=sQuery(id+"F0.wireOp",EDGE,"E7");Q0=makeQuery(id+"F31.boolean.opBoolean","MERGE",FACE,{"derivedFrom":[makeQuery(id+"F7.opExtrude","SWEPT_FACE",FACE,{"disambiguationData":[OSD([subQ0])]}),makeQuery(id+"F31.opExtrude","SWEPT_FACE",FACE,{"disambiguationData":[OSD([subQ0,sQuery(id+"F0.wireOp",EDGE,"E8"),sQuery(id+"F0.wireOp",EDGE,"E34")])]})]});}
            var sketch = newSketch(context, id + "F32", { "sketchPlane" : qUnion([Q0])});
            skLineSegment(sketch, "E66.bottom", {"start": v(6.61, 3.8) * mm, "end": v(1.11, 3.8) * mm});
            skLineSegment(sketch, "E66.top", {"start": v(6.61, 5.6) * mm, "end": v(1.11, 5.6) * mm});
            skLineSegment(sketch, "E66.left", {"start": v(6.61, 3.8) * mm, "end": v(6.61, 5.6) * mm});
            skLineSegment(sketch, "E66.right", {"start": v(1.11, 3.8) * mm, "end": v(1.11, 5.6) * mm});
            skLineSegment(sketch, "E67.bottom", {"start": v(6.61, 9.6) * mm, "end": v(4.21, 9.6) * mm});
            skLineSegment(sketch, "E67.top", {"start": v(6.61, 5.6) * mm, "end": v(4.21, 5.6) * mm});
            skLineSegment(sketch, "E67.left", {"start": v(6.61, 9.6) * mm, "end": v(6.61, 5.6) * mm});
            skLineSegment(sketch, "E67.right", {"start": v(4.21, 9.6) * mm, "end": v(4.21, 5.6) * mm});
            skSolve(sketch);
        }
        {
            var Q0;
            Q0=makeQuery(id+"F32.imprint","IMPRINT",FACE,{"disambiguationData":[TD([[makeQuery(id+"F32.imprint","IMPRINT",EDGE,{"derivedFrom":sQuery(id+"F32.wireOp",EDGE,"E67.bottom")}),1.0]])]});
            var Q1;
            Q1=makeQuery(id+"F32.imprint","IMPRINT",FACE,{"disambiguationData":[TD([[makeQuery(id+"F32.imprint","IMPRINT",EDGE,{"derivedFrom":sQuery(id+"F32.wireOp",EDGE,"E66.bottom")}),-1.0]])]});
            extrude(context, id + "F33", {"entities" : qUnion([Q0, Q1]), "operationType" : NewBodyOperationType.REMOVE, "oppositeDirection" : true, "depth" : 7.3 * mm, "offsetDistance" : 25 * mm});
        }
    });
